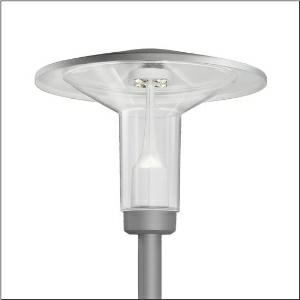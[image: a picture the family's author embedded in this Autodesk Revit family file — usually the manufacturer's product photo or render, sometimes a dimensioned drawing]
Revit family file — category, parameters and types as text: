
# Revit family: laterne_iq___p1_0a_5xa5255bf14h_d88c
name_source: partatom
category: Lighting Fixtures
units: mm (PartAtom-declared; Revit-internal decimal feet)

## family parameters
Cut with Voids When Loaded = No
Host = Face
Light Source = No
Part Type = Normal
Room Calculation Point = No
Round Connector Dimension = Use Diameter
Shared = No

## types (1)
- --- (1 x LED, 1510 lm, 12.9 W, 2200K)
    Apparent Load = 13 VA
    CIE Flux Codes = 35 64 91 96 100
    Color Rendering = 70
    Color Temperature = 2200K
    Default Elevation = 1800 mm
    Description = Lantern iQ, mast luminaire, Module 540 iQ-SR, primary light control with 3 zone facetted reflector, of plastic, silver coated, highly specular, structured, primary optical cover: cover, of PMMA, transparent, light distribution: P1.0a, light emission: direct distribution, primary light characteristic: strongly asymmetric, installation type: post-top, LED, High Power LED, rated luminous flux: 1.510lm, luminous efficacy: 117lm/W, light colour: 722, colour temperature: 2200K, control gear: iQ Street-Remote, control: pre-setting: logarithmic dimming characteristic, Street-Remote, Auto-Match, Temp-Guard, Lumen-Switch, Night-Set, Smart-Wire, Light-Fading, Desk-Remote (wireless, voltage-free reading and setting of iQ features in the workshop via application-optimized NFC function/RFID function), optimised constant luminous flux control (CLO 2.0), with terminal, 6-pole, max. 2.5mm², mains connection: 230..240V, AC, 50/60Hz, start of lifetime: 13W, end of service life: 13W, reduction: 6W, luminaire housing, upper part, of glass-fibre reinforced polyester, coated, Siteco® metallic grey (DB 702S), diameter: 750mm, height: 583mm, spigot size: d x l = 76 x 70mm (post-top) | with reducer (optional accessory) 60 x 70mm, mounting height: 3..5m, post-top mast mounting element, of diecast aluminium, coated, Siteco® metallic grey (DB 702S), Module 540 iQ-SR, traffic white (RAL 9016), equipment: standard, protection rating (complete): IP65, insulation class (complete): insulation class II (safety insulation), certification: CE, ENEC, VDE, packaging unit: 1 piece

Light Distribution: P1.0a
    Height = 583 mm
    Lamp = 1 x LED
    Lamp Light Flux = 1510 lm
    Lamp Power = 12.9 W
    Lamp count = 1
    Length = 750 mm
    Luminous efficacy = 117 lm/W
    Manufacturer = Siteco
    ModVariant = No
    Model = 5XA5255BF14H
    Number of Poles = 1
    OnlyDefault = Yes
    Power Factor = 1
    Product Name = Laterne iQ | P1.0a
    Product group = mast luminaire | pylon top
    ProductGroupID = 6100
    Protection Class = Protection class II
    Protection Degree = IP 65
    RLX_Detail_Level = 1
    RLX_Emergency_Light_Flux = 0 lm
    RLX_Emergency_Type = 0
    RLX_Emergency_Type_DB = No
    RlxData = <blob elided: 74109 chars, md5=9b014f60>
    Socket = socket
    Standby Power = 0 W
    System Light Flux = 1510 lm
    System Power = 13 W
    Type Comments = factory setting: luminous flux: 100 % | dim-lin: 254 | 516 mA
    Type Image = l_1006050.jpg
    URL = http://relux.com
    VarID = @adj_182003
    Voltage = 0 V
    Weight = 0.00 kg
    Width = 0 mm  [stored 0 ft]

note: [stored X ft] marks values corroborated as IEEE doubles in the binary element streams (Revit-internal decimal feet)

## geometry (parser evidence)
native form markers: Blend x4, Sweep x12
no freeform markers — native parametric forms only
